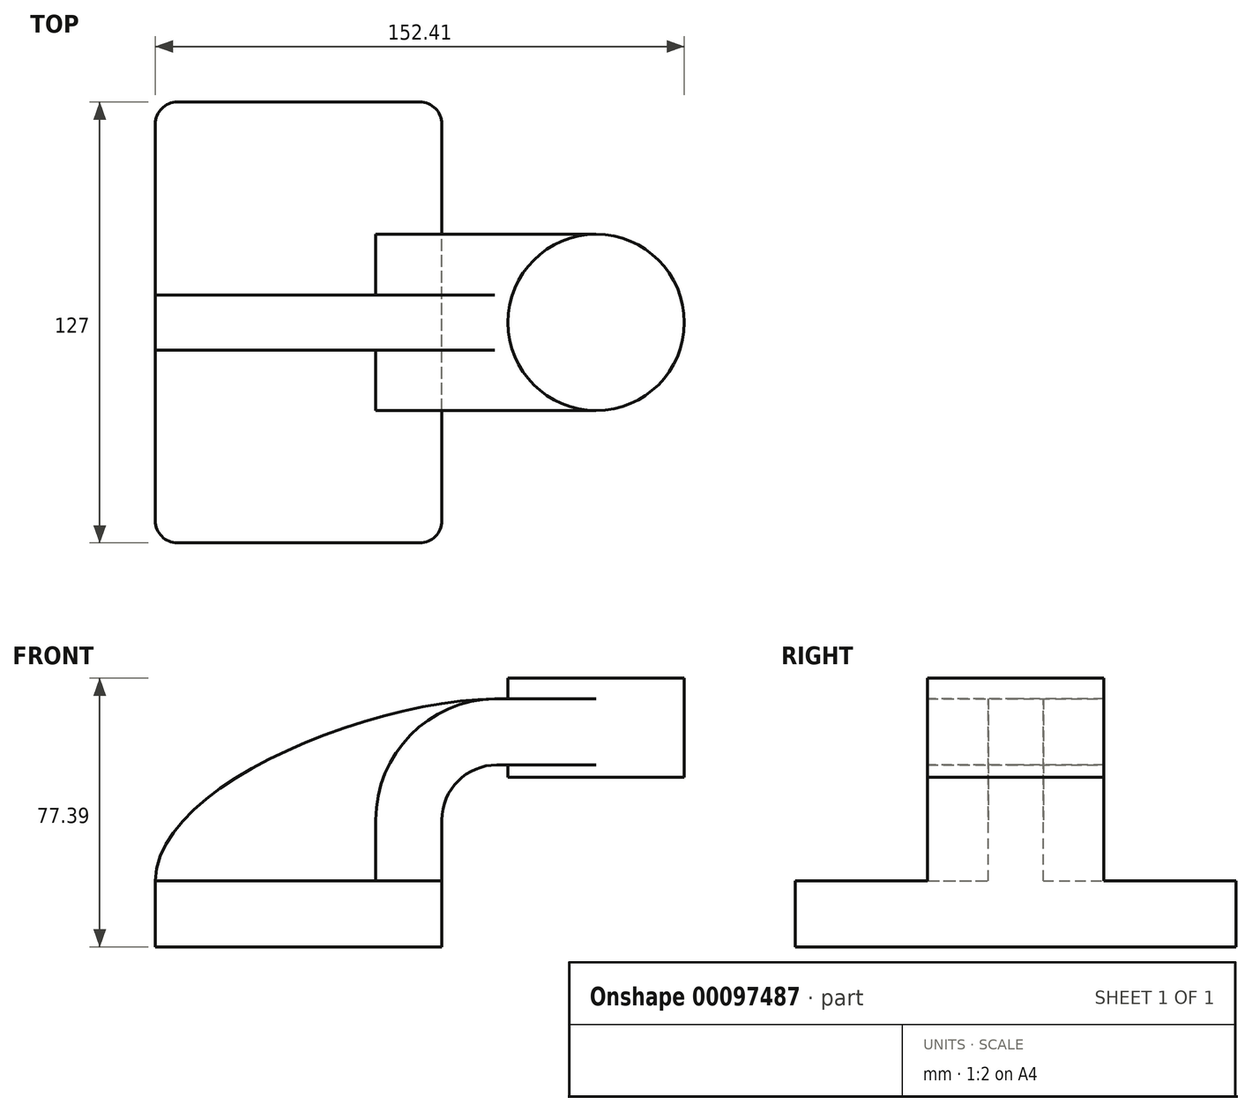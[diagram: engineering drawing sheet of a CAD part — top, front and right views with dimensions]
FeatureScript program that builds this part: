
annotation { "Feature Type Name" : "Feature", "Feature Type Description" : "" }
export const myFeature = defineFeature(function(context is Context, id is Id, definition is map)
    precondition{}
    {
        {
            var Q0;
            Q0=qCreatedBy(makeId("Front.planeOp"),FACE);
            var sketch = newSketch(context, id + "F0", { "sketchPlane" : qUnion([Q0])});
            skLineSegment(sketch, "E0.bottom", {"start": v(-41.28, -9.53) * mm, "end": v(41.28, -9.53) * mm});
            skLineSegment(sketch, "E0.top", {"start": v(-41.28, 9.53) * mm, "end": v(41.28, 9.53) * mm});
            skLineSegment(sketch, "E0.left", {"start": v(-41.28, -9.53) * mm, "end": v(-41.28, 9.53) * mm});
            skLineSegment(sketch, "E0.right", {"start": v(41.28, -9.53) * mm, "end": v(41.28, 9.53) * mm});
            skPoint(sketch, "E0.middle", {"position": v(0, 0) * mm});
            skLineSegment(sketch, "E1.bottom", {"start": v(60.32, 39.28) * mm, "end": v(111.13, 39.28) * mm});
            skLineSegment(sketch, "E1.top", {"start": v(60.32, 67.86) * mm, "end": v(111.12, 67.86) * mm});
            skLineSegment(sketch, "E1.left", {"start": v(60.32, 39.28) * mm, "end": v(60.32, 67.86) * mm});
            skLineSegment(sketch, "E1.right", {"start": v(111.13, 39.28) * mm, "end": v(111.12, 67.86) * mm});
            skPoint(sketch, "E1.middle", {"position": v(85.72, 53.57) * mm});
            skLineSegment(sketch, "E2", {"start": v(41.28, 9.53) * mm, "end": v(41.28, 27) * mm});
            skArc(sketch, "E3", {"start": v(41.27, 27) * mm, "mid": v(45.92, 38.23) * mm, "end": v(57.15, 42.88) * mm});
            skLineSegment(sketch, "E4", {"start": v(57.15, 42.88) * mm, "end": v(85.72, 42.88) * mm});
            skLineSegment(sketch, "E5.0", {"start": v(57.15, 61.93) * mm, "end": v(85.72, 61.93) * mm});
            skArc(sketch, "E5.1", {"start": v(22.23, 27) * mm, "mid": v(32.45, 51.7) * mm, "end": v(57.15, 61.93) * mm});
            skLineSegment(sketch, "E5.2", {"start": v(22.22, 9.53) * mm, "end": v(22.22, 27) * mm});
            skLineSegment(sketch, "E6", {"start": v(85.72, 42.88) * mm, "end": v(85.72, 61.93) * mm});
            skLineSegment(sketch, "E7", {"start": v(85.72, 61.93) * mm, "end": v(85.72, 67.86) * mm});
            skLineSegment(sketch, "E8", {"start": v(85.72, 42.88) * mm, "end": v(85.72, 39.28) * mm});
            skFitSpline(sketch, "E9", {"points": [v(-41.28, 9.53) * mm, v(57.15, 61.93) * mm], "startDerivative": vector(0.21, 81.97) * mm, "endDerivative": vector(109.08, 0.54) * mm});
            skSolve(sketch);
        }
        {
            var Q0;
            Q0=makeQuery(id+"F0.imprint","IMPRINT",FACE,{"disambiguationData":[TD([[makeQuery(id+"F0.imprint","IMPRINT",EDGE,{"derivedFrom":sQuery(id+"F0.wireOp",EDGE,"E0.bottom")}),1.0]])]});
            extrude(context, id + "F1", {"entities" : qUnion([Q0]), "endBound" : BoundingType.SYMMETRIC, "depth" : 127 * mm});
        }
        {
            var Q0;
            {var subQ1=sQuery(id+"F0.wireOp",EDGE,"E2");Q0=makeQuery(id+"F0.imprint","IMPRINT",FACE,{"disambiguationData":[TD([[makeQuery(id+"F0.imprint","IMPRINT",EDGE,{"derivedFrom":subQ1}),1.0]])]});}
            var Q1;
            {var subQ5=sQuery(id+"F0.wireOp",EDGE,"E6");Q1=makeQuery(id+"F0.imprint","IMPRINT",FACE,{"disambiguationData":[TD([[makeQuery(id+"F0.imprint","IMPRINT",EDGE,{"derivedFrom":subQ5}),1.0]])]});}
            extrude(context, id + "F2", {"entities" : qUnion([Q0, Q1]), "operationType" : NewBodyOperationType.ADD, "endBound" : BoundingType.SYMMETRIC, "depth" : 50.8 * mm});
        }
        {
            var Q0;
            {var subQ3=sQuery(id+"F0.wireOp",EDGE,"E5.2");Q0=makeQuery(id+"F0.imprint","IMPRINT",FACE,{"disambiguationData":[TD([[makeQuery(id+"F0.imprint","IMPRINT",EDGE,{"derivedFrom":subQ3}),1.0]])]});}
            extrude(context, id + "F3", {"entities" : qUnion([Q0]), "operationType" : NewBodyOperationType.ADD, "endBound" : BoundingType.SYMMETRIC, "depth" : 15.88 * mm});
        }
        {
            var Q0;
            {var subQ0=sQuery(id+"F0.wireOp",EDGE,"E1.right");Q0=makeQuery(id+"F0.imprint","IMPRINT",FACE,{"disambiguationData":[TD([[makeQuery(id+"F0.imprint","IMPRINT",EDGE,{"derivedFrom":subQ0}),1.0]])]});}
            var Q1;
            Q1=sQuery(id+"F0.wireOp",EDGE,"E6");
            revolve(context, id + "F4", {"operationType" : NewBodyOperationType.ADD, "entities" : qUnion([Q0]), "axis" : qUnion([Q1]), "revolveType" : RevolveType.FULL});
        }
        {
            var Q0;
            Q0=makeQuery(id+"F1.opExtrude","CAP_EDGE",EDGE,{"disambiguationData":[OSD([sQuery(id+"F0.wireOp",EDGE,"E0.left")])],"isStart":false});
            var Q1;
            Q1=makeQuery(id+"F1.opExtrude","CAP_EDGE",EDGE,{"disambiguationData":[OSD([sQuery(id+"F0.wireOp",EDGE,"E0.left")])],"isStart":true});
            var Q2;
            Q2=makeQuery(id+"F1.opExtrude","CAP_EDGE",EDGE,{"disambiguationData":[OSD([sQuery(id+"F0.wireOp",EDGE,"E0.right")])],"isStart":true});
            var Q3;
            Q3=makeQuery(id+"F1.opExtrude","CAP_EDGE",EDGE,{"disambiguationData":[OSD([sQuery(id+"F0.wireOp",EDGE,"E0.right")])],"isStart":false});
            fillet(context, id + "F5", {"entities" : qUnion([Q0, Q1, Q2, Q3]), "radius" : 6.35 * mm, "tangentPropagation" : true, "allowEdgeOverflow" : false});
        }
    });
